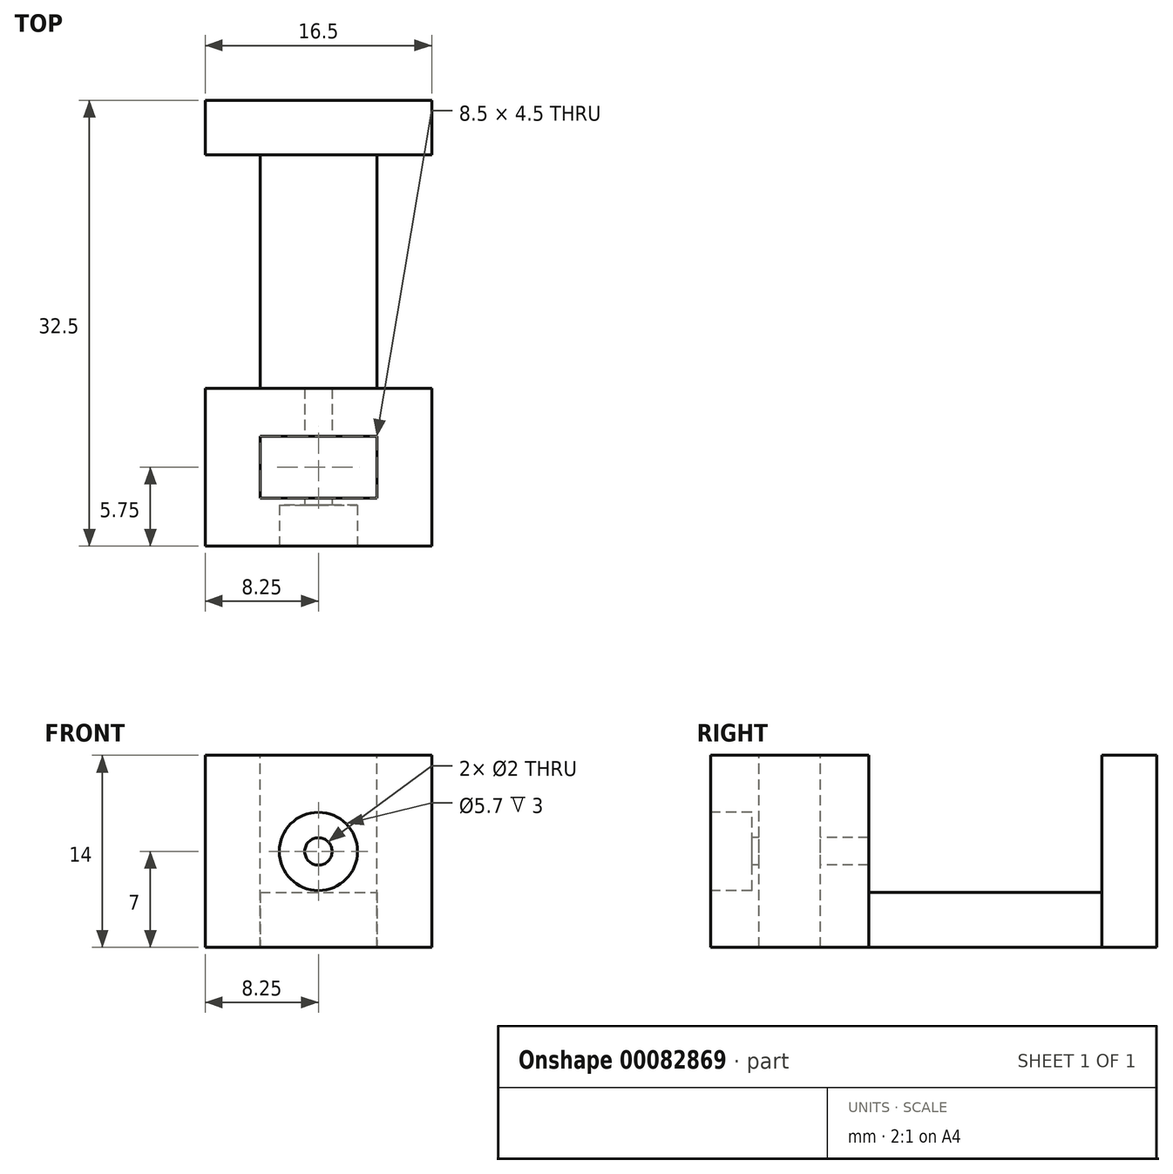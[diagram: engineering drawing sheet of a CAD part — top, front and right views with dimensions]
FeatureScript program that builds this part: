
annotation { "Feature Type Name" : "Feature", "Feature Type Description" : "" }
export const myFeature = defineFeature(function(context is Context, id is Id, definition is map)
    precondition{}
    {
        {
            var Q0;
            Q0=qCreatedBy(makeId("Top.planeOp"),FACE);
            var sketch = newSketch(context, id + "F0", { "sketchPlane" : qUnion([Q0])});
            skLineSegment(sketch, "E0.bottom", {"start": v(-8.25, 16.25) * mm, "end": v(8.25, 16.25) * mm});
            skLineSegment(sketch, "E0.top", {"start": v(-8.25, -16.25) * mm, "end": v(8.25, -16.25) * mm});
            skLineSegment(sketch, "E0.left", {"start": v(-8.25, 16.25) * mm, "end": v(-8.25, -16.25) * mm});
            skLineSegment(sketch, "E0.right", {"start": v(8.25, 16.25) * mm, "end": v(8.25, -16.25) * mm});
            skSolve(sketch);
        }
        {
            var Q0;
            Q0=qSketchRegion(id+"F0",true);
            extrude(context, id + "F1", {"entities" : qUnion([Q0]), "depth" : 14 * mm});
        }
        {
            var Q0;
            Q0=makeQuery(id+"F1.opExtrude","CAP_FACE",FACE,{"disambiguationData":[OSD([sQuery(id+"F0.wireOp",EDGE,"E0.bottom"),sQuery(id+"F0.wireOp",EDGE,"E0.top"),sQuery(id+"F0.wireOp",EDGE,"E0.left"),sQuery(id+"F0.wireOp",EDGE,"E0.right")])],"isStart":false});
            var sketch = newSketch(context, id + "F2", { "sketchPlane" : qUnion([Q0])});
            skLineSegment(sketch, "E1.bottom", {"start": v(-8.25, -4.25) * mm, "end": v(8.25, -4.25) * mm, "construction": true});
            skLineSegment(sketch, "E1.top", {"start": v(-8.25, -16.25) * mm, "end": v(8.25, -16.25) * mm, "construction": true});
            skLineSegment(sketch, "E1.left", {"start": v(-8.25, -4.25) * mm, "end": v(-8.25, -16.25) * mm, "construction": true});
            skLineSegment(sketch, "E1.right", {"start": v(8.25, -4.25) * mm, "end": v(8.25, -16.25) * mm, "construction": true});
            skSolve(sketch);
        }
        {
            var Q0;
            Q0=makeQuery(id+"F2.imprint","IMPRINT",FACE,{"disambiguationData":[TD([[makeQuery(id+"F2.imprint","IMPRINT",EDGE,{"derivedFrom":makeQuery(id+"F1.opExtrude","CAP_EDGE",EDGE,{"disambiguationData":[OSD([sQuery(id+"F0.wireOp",EDGE,"E0.bottom")])],"isStart":false})}),-1.0]])]});
            var sketch = newSketch(context, id + "F3", { "sketchPlane" : qUnion([Q0])});
            skLineSegment(sketch, "E2.bottom", {"start": v(-8.25, 12.25) * mm, "end": v(8.25, 12.25) * mm});
            skLineSegment(sketch, "E2.top", {"start": v(-8.25, -4.75) * mm, "end": v(8.25, -4.75) * mm});
            skLineSegment(sketch, "E2.left", {"start": v(-8.25, 12.25) * mm, "end": v(-8.25, -4.75) * mm});
            skLineSegment(sketch, "E2.right", {"start": v(8.25, 12.25) * mm, "end": v(8.25, -4.75) * mm});
            skSolve(sketch);
        }
        {
            var Q0;
            Q0=qSketchRegion(id+"F3",true);
            extrude(context, id + "F4", {"entities" : qUnion([Q0]), "operationType" : NewBodyOperationType.REMOVE, "oppositeDirection" : true, "depth" : 10 * mm});
        }
        {
            var Q0;
            Q0=makeQuery(id+"F1.opExtrude","CAP_FACE",FACE,{"disambiguationData":[OSD([sQuery(id+"F0.wireOp",EDGE,"E0.bottom"),sQuery(id+"F0.wireOp",EDGE,"E0.top"),sQuery(id+"F0.wireOp",EDGE,"E0.left"),sQuery(id+"F0.wireOp",EDGE,"E0.right")])],"isStart":true});
            var sketch = newSketch(context, id + "F5", { "sketchPlane" : qUnion([Q0])});
            skLineSegment(sketch, "E3.bottom", {"start": v(-8.25, -12.25) * mm, "end": v(-4.25, -12.25) * mm});
            skLineSegment(sketch, "E3.top", {"start": v(-8.25, 4.75) * mm, "end": v(-4.25, 4.75) * mm});
            skLineSegment(sketch, "E3.left", {"start": v(-8.25, -12.25) * mm, "end": v(-8.25, 4.75) * mm});
            skLineSegment(sketch, "E3.right", {"start": v(-4.25, -12.25) * mm, "end": v(-4.25, 4.75) * mm});
            skLineSegment(sketch, "E4.bottom", {"start": v(4.25, -12.25) * mm, "end": v(8.25, -12.25) * mm});
            skLineSegment(sketch, "E4.top", {"start": v(4.25, 4.75) * mm, "end": v(8.25, 4.75) * mm});
            skLineSegment(sketch, "E4.left", {"start": v(4.25, -12.25) * mm, "end": v(4.25, 4.75) * mm});
            skLineSegment(sketch, "E4.right", {"start": v(8.25, -12.25) * mm, "end": v(8.25, 4.75) * mm});
            skSolve(sketch);
        }
        {
            var Q0;
            Q0=qSketchRegion(id+"F5",true);
            extrude(context, id + "F6", {"entities" : qUnion([Q0]), "operationType" : NewBodyOperationType.REMOVE, "endBound" : BoundingType.THROUGH_ALL, "oppositeDirection" : true, "depth" : 25 * mm});
        }
        {
            var Q0;
            Q0=makeQuery(id+"F2.imprint","IMPRINT",FACE,{"disambiguationData":[TD([[makeQuery(id+"F2.imprint","IMPRINT",EDGE,{"derivedFrom":makeQuery(id+"F1.opExtrude","CAP_EDGE",EDGE,{"disambiguationData":[OSD([sQuery(id+"F0.wireOp",EDGE,"E0.bottom")])],"isStart":false})}),-1.0]])]});
            var sketch = newSketch(context, id + "F7", { "sketchPlane" : qUnion([Q0])});
            skLineSegment(sketch, "E5.bottom", {"start": v(-4.25, -8.25) * mm, "end": v(4.25, -8.25) * mm});
            skLineSegment(sketch, "E5.top", {"start": v(-4.25, -12.75) * mm, "end": v(4.25, -12.75) * mm});
            skLineSegment(sketch, "E5.left", {"start": v(-4.25, -8.25) * mm, "end": v(-4.25, -12.75) * mm});
            skLineSegment(sketch, "E5.right", {"start": v(4.25, -8.25) * mm, "end": v(4.25, -12.75) * mm});
            skSolve(sketch);
        }
        {
            var Q0;
            Q0=qSketchRegion(id+"F7",true);
            extrude(context, id + "F8", {"entities" : qUnion([Q0]), "operationType" : NewBodyOperationType.REMOVE, "endBound" : BoundingType.THROUGH_ALL, "oppositeDirection" : true, "depth" : 25 * mm});
        }
        {
            var Q0;
            Q0=makeQuery(id+"F1.opExtrude","SWEPT_FACE",FACE,{"disambiguationData":[OSD([sQuery(id+"F0.wireOp",EDGE,"E0.top")])]});
            var sketch = newSketch(context, id + "F9", { "sketchPlane" : qUnion([Q0])});
            skLineSegment(sketch, "E6", {"start": v(0, 14) * mm, "end": v(0, 0) * mm, "construction": true});
            skCircle(sketch, "E7", {"center": v(0, 7) * mm, "radius": 2.85 * mm});
            skSolve(sketch);
        }
        {
            var Q0;
            Q0=qSketchRegion(id+"F9",true);
            extrude(context, id + "F10", {"entities" : qUnion([Q0]), "operationType" : NewBodyOperationType.REMOVE, "oppositeDirection" : true, "depth" : 3 * mm});
        }
        {
            var Q0;
            Q0=makeQuery(id+"F10.boolean.opBoolean","COPY",FACE,{"derivedFrom":makeQuery(id+"F10.opExtrude","CAP_FACE",FACE,{"disambiguationData":[OSD([sQuery(id+"F9.wireOp",EDGE,"E7")])],"isStart":false})});
            var sketch = newSketch(context, id + "F11", { "sketchPlane" : qUnion([Q0])});
            skCircle(sketch, "E8", {"center": v(0, 7) * mm, "radius": 1 * mm});
            skSolve(sketch);
        }
        {
            var Q0;
            Q0=qSketchRegion(id+"F11",true);
            extrude(context, id + "F12", {"entities" : qUnion([Q0]), "operationType" : NewBodyOperationType.REMOVE, "oppositeDirection" : true, "depth" : 10 * mm});
        }
    });
